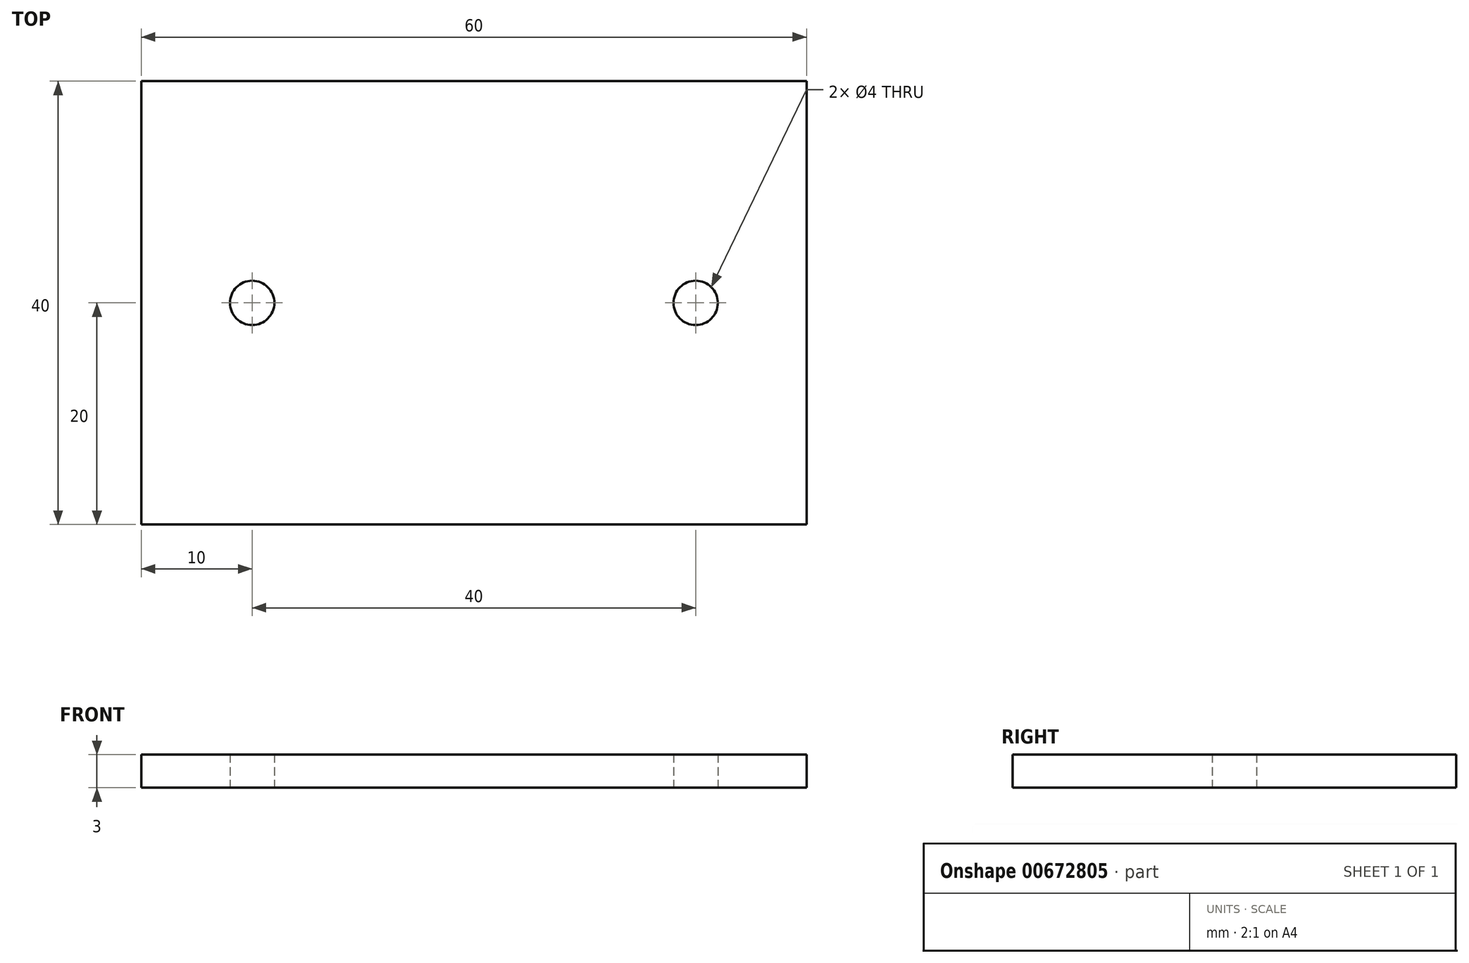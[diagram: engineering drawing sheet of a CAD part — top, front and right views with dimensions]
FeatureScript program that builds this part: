
annotation { "Feature Type Name" : "Feature", "Feature Type Description" : "" }
export const myFeature = defineFeature(function(context is Context, id is Id, definition is map)
    precondition{}
    {
        {
            var Q0;
            Q0=qCreatedBy(makeId("Top.planeOp"),FACE);
            var sketch = newSketch(context, id + "F0", { "sketchPlane" : qUnion([Q0])});
            skLineSegment(sketch, "E0.bottom", {"start": v(-30, 20) * mm, "end": v(30, 20) * mm});
            skLineSegment(sketch, "E0.top", {"start": v(-30, -20) * mm, "end": v(30, -20) * mm});
            skLineSegment(sketch, "E0.left", {"start": v(-30, 20) * mm, "end": v(-30, -20) * mm});
            skLineSegment(sketch, "E0.right", {"start": v(30, 20) * mm, "end": v(30, -20) * mm});
            skPoint(sketch, "E0.middle", {"position": v(0, 0) * mm});
            skCircle(sketch, "E1", {"center": v(-20, 0) * mm, "radius": 2 * mm});
            skCircle(sketch, "E2", {"center": v(20, 0) * mm, "radius": 2 * mm});
            skLineSegment(sketch, "E3", {"start": v(-20, 0) * mm, "end": v(20, 0) * mm});
            skSolve(sketch);
        }
        {
            var Q0;
            Q0=makeQuery(id+"F0.imprint","IMPRINT",FACE,{"disambiguationData":[TD([[makeQuery(id+"F0.imprint","IMPRINT",EDGE,{"derivedFrom":sQuery(id+"F0.wireOp",EDGE,"E0.bottom")}),-1.0]])]});
            extrude(context, id + "F1", {"entities" : qUnion([Q0]), "depth" : 3 * mm, "offsetDistance" : 25 * mm});
        }
    });
